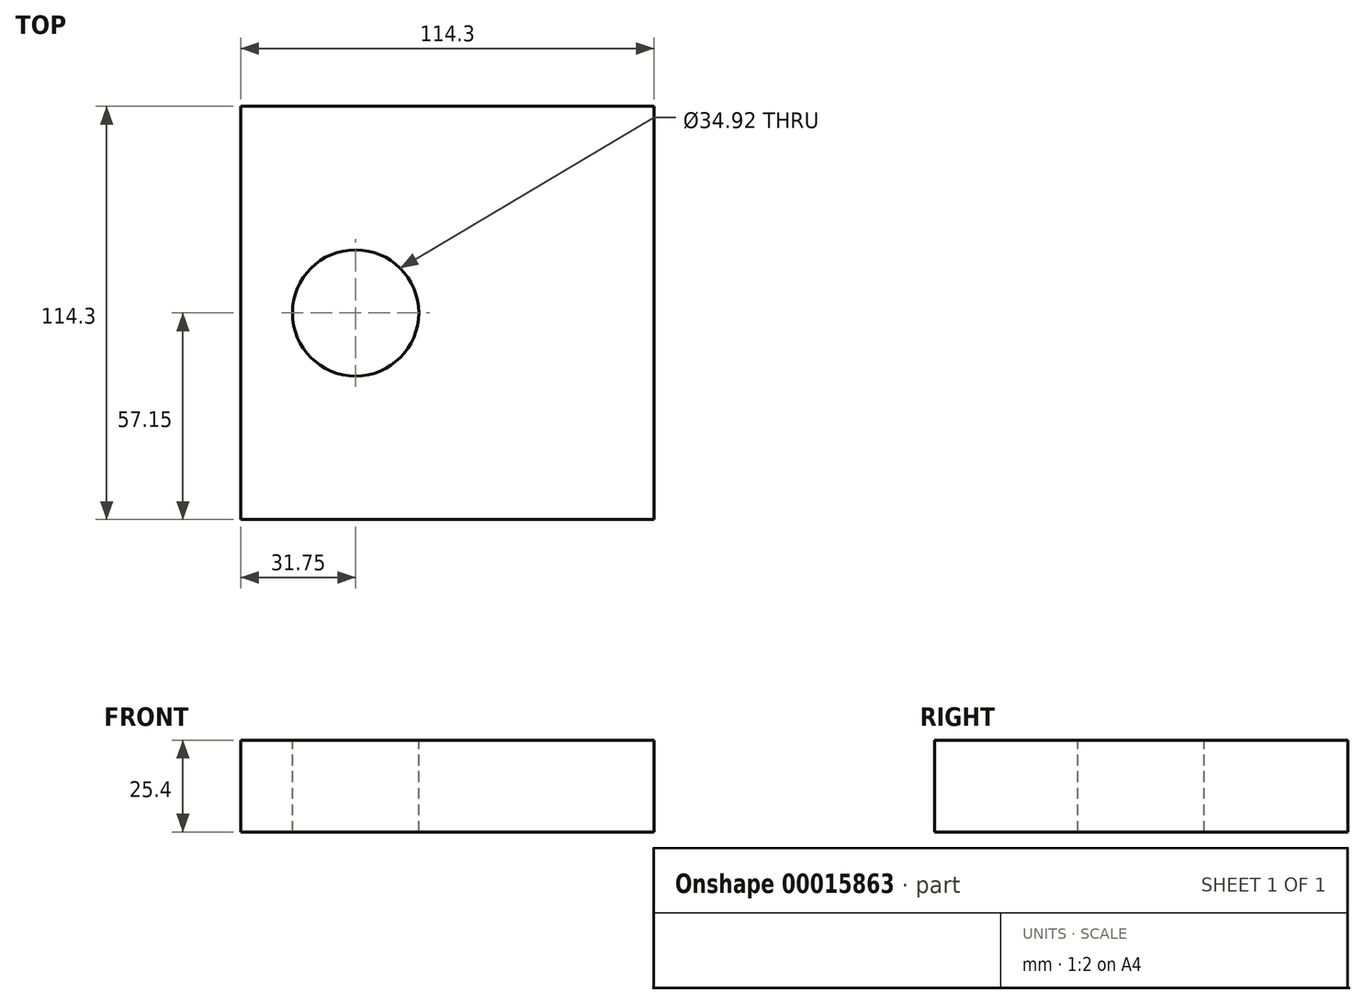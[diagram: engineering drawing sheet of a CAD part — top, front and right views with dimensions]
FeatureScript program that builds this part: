
annotation { "Feature Type Name" : "Feature", "Feature Type Description" : "" }
export const myFeature = defineFeature(function(context is Context, id is Id, definition is map)
    precondition{}
    {
        {
            var Q0;
            Q0=qCreatedBy(makeId("Top.planeOp"),FACE);
            var sketch = newSketch(context, id + "F0", { "sketchPlane" : qUnion([Q0])});
            skLineSegment(sketch, "E0", {"start": v(-57.15, 57.15) * mm, "end": v(57.15, 57.15) * mm});
            skLineSegment(sketch, "E1", {"start": v(57.15, 57.15) * mm, "end": v(57.15, -57.15) * mm});
            skLineSegment(sketch, "E2", {"start": v(57.15, -57.15) * mm, "end": v(-57.15, -57.15) * mm});
            skLineSegment(sketch, "E3", {"start": v(-57.15, -57.15) * mm, "end": v(-57.15, 57.15) * mm});
            skLineSegment(sketch, "E4", {"start": v(-57.15, 57.15) * mm, "end": v(57.15, -57.15) * mm, "construction": true});
            skSolve(sketch);
        }
        {
            var Q0;
            Q0 = qSketchRegion(id + "F0", true);
            extrude(context, id + "F1", {"entities" : qUnion([Q0]), "depth" : 25.4 * mm});
        }
        {
            var Q0;
            Q0=makeQuery(id+"F1.opExtrude","CAP_FACE",FACE,{"disambiguationData":[OSD([sQuery(id+"F0.wireOp",EDGE,"E0"),sQuery(id+"F0.wireOp",EDGE,"E1"),sQuery(id+"F0.wireOp",EDGE,"E2"),sQuery(id+"F0.wireOp",EDGE,"E3")])],"isStart":false});
            var sketch = newSketch(context, id + "F2", { "sketchPlane" : qUnion([Q0])});
            skCircle(sketch, "E5", {"center": v(-25.4, 0) * mm, "radius": 17.46 * mm});
            skLineSegment(sketch, "E6", {"start": v(-25.4, 0) * mm, "end": v(0, 0) * mm, "construction": true});
            skSolve(sketch);
        }
        {
            var Q0;
            Q0=makeQuery(id+"F2.imprint","IMPRINT",FACE,{"disambiguationData":[TD([[makeQuery(id+"F2.imprint","IMPRINT",EDGE,{"derivedFrom":sQuery(id+"F2.wireOp",EDGE,"E5")}),1.0]])]});
            extrude(context, id + "F3", {"entities" : qUnion([Q0]), "operationType" : NewBodyOperationType.REMOVE, "oppositeDirection" : true, "depth" : 25.4 * mm});
        }
    });
